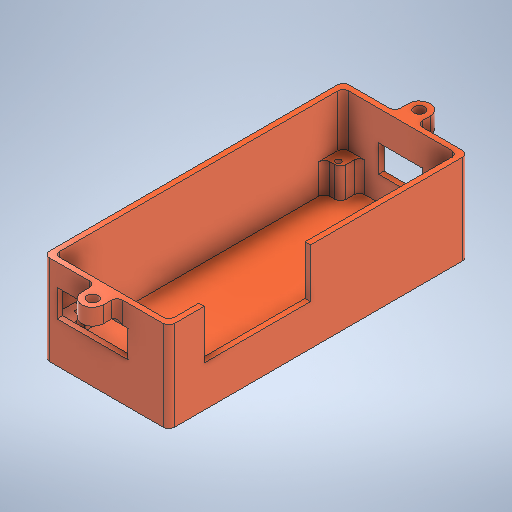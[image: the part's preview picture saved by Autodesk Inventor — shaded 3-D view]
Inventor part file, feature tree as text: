
AUTODESK INVENTOR PART (.ipt)
format: ipt  version: 2025.2 (Build 292293000, 293)  size: 427,520 bytes
history: native  units: mm
features: extrude x7, sketch x7, fillet x2
ambient origin geometry x8: Origin, YZ Plane, XZ Plane, XY Plane, X Axis, Y Axis, Z Axis, Center Point
bodies: Solid1 (feature_tree)
feature tree (16):
  extrude  "Extrusion1"  Depth=110.0mm
  extrude  "Extrusion2"  Depth=42.0mm
  extrude  "Extrusion5"  Depth=30.0mm TaperAngle=0.0deg
  extrude  "Extrusion6"  Depth=58.0mm
  extrude  "Extrusion7"  Depth=16.0mm
  sketch  "Sketch9"  dims[d29=15.0mm d30=10.0mm d32=12.0mm]
  extrude  "Extrusion10"  Depth=10.0mm
  fillet  "Fillet2"  Radius=12.0mm
  extrude  "Extrusion11"  Depth=5.0mm
  fillet  "Fillet6"  Radius=10.0mm
  sketch  "Sketch1"  dims[d0=46.0mm d1=110.0mm]
  sketch  "Sketch2"  dims[d2=3.0mm d3=0.0mm d4=42.0mm]
  sketch  "Sketch5"  dims[d5=106.0mm d6=30.0mm d7=0.0mm]
  sketch  "Sketch6"  dims[d24=13.0mm d25=58.0mm]
  sketch  "Sketch7"  dims[d26=18.0mm d27=0.0mm d28=16.0mm]
  sketch  "Sketch11"  dims[d33=15.0mm d34=0.0mm d35=5.0mm d36=10.0mm d37=15.0mm d38=26.0mm d39=15.0mm d40=0.0mm d77=4.0mm d78=5.0mm d79=8.0mm d80=4.0mm d81=4.0mm d82=4.0mm d83=5.0mm d84=8.0mm d85=4.0mm d86=6.0mm d87=0.0mm d88=2.0mm d95=2.0mm d96=2.0mm d97=2.0mm d98=2.0mm d99=95.5mm d100=35.0mm d101=47.75mm d102=17.5mm d103=6.0mm d104=7.0mm d105=6.0mm d106=7.0mm d107=6.0mm d108=7.0mm d109=6.0mm d110=7.0mm d111=11.0mm d112=0.0mm d114=2.0mm d53=0.5mm d54=0.872665mm d55=0.5mm d56=0.872665mm]
